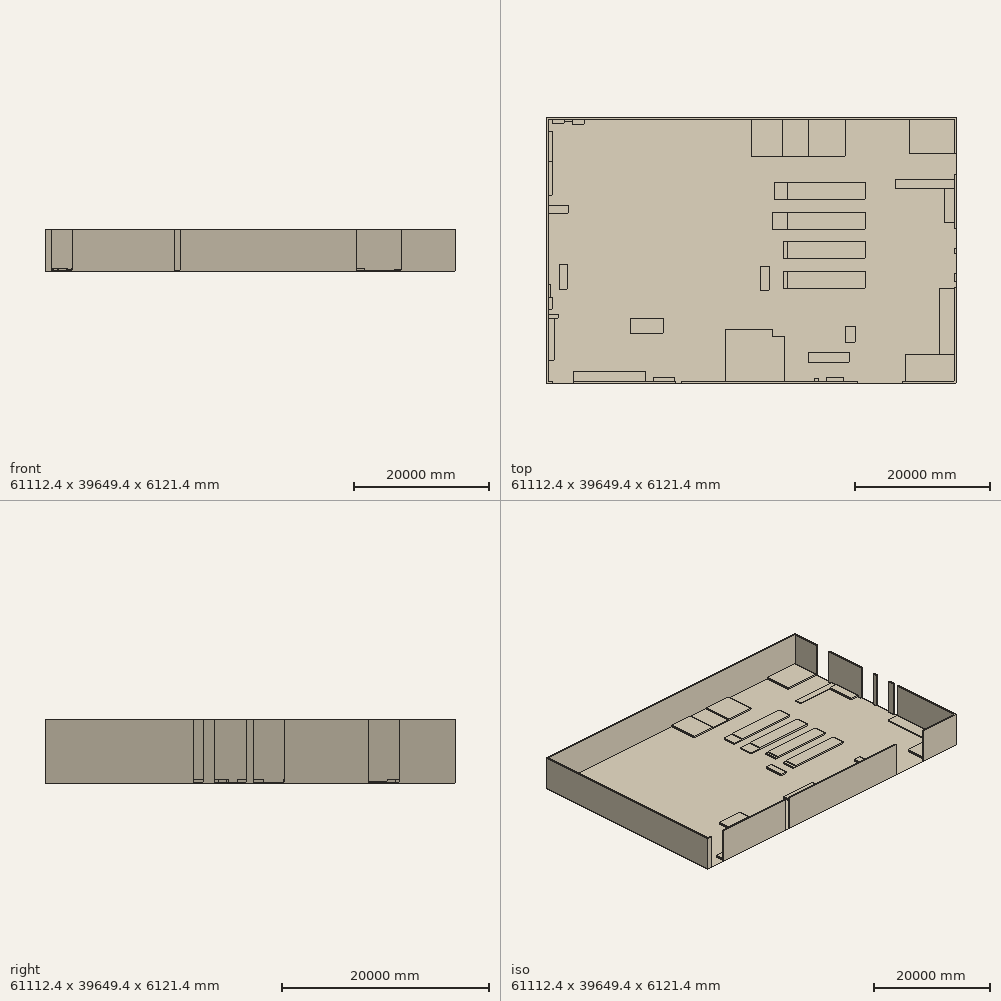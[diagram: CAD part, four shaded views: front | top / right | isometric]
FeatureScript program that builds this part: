
annotation { "Feature Type Name" : "Feature", "Feature Type Description" : "" }
export const myFeature = defineFeature(function(context is Context, id is Id, definition is map)
    precondition{}
    {
        {
            var Q0;
            Q0=qCreatedBy(makeId("Top.planeOp"),FACE);
            var sketch = newSketch(context, id + "F0", { "sketchPlane" : qUnion([Q0])});
            skLineSegment(sketch, "E0.bottom", {"start": v(30556.2, 19824.7) * mm, "end": v(-30556.2, 19824.7) * mm});
            skLineSegment(sketch, "E0.top", {"start": v(30556.2, -19824.7) * mm, "end": v(22479, -19824.7) * mm});
            skLineSegment(sketch, "E0.left", {"start": v(30556.2, 19824.7) * mm, "end": v(30556.2, 14439.9) * mm});
            skLineSegment(sketch, "E0.right", {"start": v(-30556.2, 19824.7) * mm, "end": v(-30556.2, -19824.7) * mm});
            skPoint(sketch, "E0.middle", {"position": v(0, 0) * mm});
            skPoint(sketch, "E1", {"position": v(30556.2, 18148.3) * mm});
            skPoint(sketch, "E2", {"position": v(30556.2, 15100.3) * mm});
            skPoint(sketch, "E3", {"position": v(30556.2, 14439.9) * mm});
            skPoint(sketch, "E4", {"position": v(30556.2, 11391.9) * mm});
            skPoint(sketch, "E5", {"position": v(30556.2, 10731.5) * mm});
            skPoint(sketch, "E6", {"position": v(30556.2, 7683.5) * mm});
            skPoint(sketch, "E7", {"position": v(30556.2, 7023.1) * mm});
            skPoint(sketch, "E8", {"position": v(30556.2, 3975.1) * mm});
            skPoint(sketch, "E9", {"position": v(30556.2, 3314.7) * mm});
            skPoint(sketch, "E10", {"position": v(30556.2, 266.7) * mm});
            skPoint(sketch, "E11", {"position": v(30556.2, -393.7) * mm});
            skPoint(sketch, "E12", {"position": v(30556.2, -3441.7) * mm});
            skPoint(sketch, "E13", {"position": v(30556.2, -4584.7) * mm});
            skPoint(sketch, "E14", {"position": v(30556.2, -5499.1) * mm});
            skPoint(sketch, "E15", {"position": v(-29641.8, -19824.7) * mm});
            skPoint(sketch, "E16", {"position": v(-26593.8, -19824.7) * mm});
            skPoint(sketch, "E17", {"position": v(-11353.8, -19824.7) * mm});
            skPoint(sketch, "E18", {"position": v(-10439.4, -19824.7) * mm});
            skPoint(sketch, "E19", {"position": v(15773.4, -19824.7) * mm});
            skPoint(sketch, "E20", {"position": v(22479, -19824.7) * mm});
            skLineSegment(sketch, "E21.0", {"start": v(30302.2, -19570.7) * mm, "end": v(22479, -19570.7) * mm});
            skLineSegment(sketch, "E21.1", {"start": v(30302.2, 19570.7) * mm, "end": v(30302.2, 14439.9) * mm});
            skLineSegment(sketch, "E21.2", {"start": v(30302.2, 19570.7) * mm, "end": v(-30302.2, 19570.7) * mm});
            skLineSegment(sketch, "E21.3", {"start": v(-30302.2, 19570.7) * mm, "end": v(-30302.2, -19570.7) * mm});
            skLineSegment(sketch, "E22", {"start": v(30556.2, 18148.3) * mm, "end": v(30302.2, 18148.3) * mm});
            skLineSegment(sketch, "E23", {"start": v(30556.2, 15100.3) * mm, "end": v(30302.2, 15100.3) * mm});
            skLineSegment(sketch, "E24", {"start": v(30556.2, 14439.9) * mm, "end": v(30302.2, 14439.9) * mm});
            skLineSegment(sketch, "E25", {"start": v(30556.2, 11391.9) * mm, "end": v(30302.2, 11391.9) * mm});
            skLineSegment(sketch, "E26", {"start": v(30556.2, 10731.5) * mm, "end": v(30302.2, 10731.5) * mm});
            skLineSegment(sketch, "E27", {"start": v(30556.2, 7683.5) * mm, "end": v(30302.2, 7683.5) * mm});
            skLineSegment(sketch, "E28", {"start": v(30556.2, 7023.1) * mm, "end": v(30302.2, 7023.1) * mm});
            skLineSegment(sketch, "E29", {"start": v(30556.2, 3975.1) * mm, "end": v(30302.2, 3975.1) * mm});
            skLineSegment(sketch, "E30", {"start": v(30556.2, 3314.7) * mm, "end": v(30302.2, 3314.7) * mm});
            skLineSegment(sketch, "E31", {"start": v(30556.2, 266.7) * mm, "end": v(30302.2, 266.7) * mm});
            skLineSegment(sketch, "E32", {"start": v(30556.2, -393.7) * mm, "end": v(30302.2, -393.7) * mm});
            skLineSegment(sketch, "E33", {"start": v(30556.2, -3441.7) * mm, "end": v(30302.2, -3441.7) * mm});
            skLineSegment(sketch, "E34", {"start": v(30556.2, -4584.7) * mm, "end": v(30302.2, -4584.7) * mm});
            skLineSegment(sketch, "E35", {"start": v(30556.2, -5499.1) * mm, "end": v(30302.2, -5499.1) * mm});
            skLineSegment(sketch, "E36", {"start": v(22479, -19824.7) * mm, "end": v(22479, -19570.7) * mm});
            skLineSegment(sketch, "E37", {"start": v(15773.4, -19824.7) * mm, "end": v(15773.4, -19570.7) * mm});
            skLineSegment(sketch, "E38", {"start": v(-10439.4, -19824.7) * mm, "end": v(-10439.4, -19570.7) * mm});
            skLineSegment(sketch, "E39", {"start": v(-11353.8, -19824.7) * mm, "end": v(-11353.8, -19570.7) * mm});
            skLineSegment(sketch, "E40", {"start": v(-26593.8, -19824.7) * mm, "end": v(-26593.8, -19570.7) * mm});
            skLineSegment(sketch, "E41", {"start": v(-29641.8, -19824.7) * mm, "end": v(-29641.8, -19570.7) * mm});
            skLineSegment(sketch, "E42.trimOffspring", {"start": v(-29641.8, -19824.7) * mm, "end": v(-30556.2, -19824.7) * mm});
            skLineSegment(sketch, "E43.trimOffspring", {"start": v(-29641.8, -19570.7) * mm, "end": v(-30302.2, -19570.7) * mm});
            skLineSegment(sketch, "E44.trimOffspring", {"start": v(-11353.8, -19824.7) * mm, "end": v(-26593.8, -19824.7) * mm});
            skLineSegment(sketch, "E45.trimOffspring", {"start": v(-11353.8, -19570.7) * mm, "end": v(-26593.8, -19570.7) * mm});
            skLineSegment(sketch, "E46.trimOffspring", {"start": v(15773.4, -19824.7) * mm, "end": v(-10439.4, -19824.7) * mm});
            skLineSegment(sketch, "E47.trimOffspring", {"start": v(15773.4, -19570.7) * mm, "end": v(-10439.4, -19570.7) * mm});
            skLineSegment(sketch, "E48.trimOffspring", {"start": v(30556.2, -5499.1) * mm, "end": v(30556.2, -19824.7) * mm});
            skLineSegment(sketch, "E49.trimOffspring", {"start": v(30302.2, -5499.1) * mm, "end": v(30302.2, -19570.7) * mm});
            skLineSegment(sketch, "E50.trimOffspring", {"start": v(30556.2, -3441.7) * mm, "end": v(30556.2, -4584.7) * mm});
            skLineSegment(sketch, "E51.trimOffspring", {"start": v(30302.2, -3441.7) * mm, "end": v(30302.2, -4584.7) * mm});
            skLineSegment(sketch, "E52.trimOffspring", {"start": v(30556.2, 266.7) * mm, "end": v(30556.2, -393.7) * mm});
            skLineSegment(sketch, "E53.trimOffspring", {"start": v(30302.2, 266.7) * mm, "end": v(30302.2, -393.7) * mm});
            skLineSegment(sketch, "E54.trimOffspring", {"start": v(30556.2, 11391.9) * mm, "end": v(30556.2, 3314.7) * mm});
            skLineSegment(sketch, "E55.trimOffspring", {"start": v(30302.2, 11391.9) * mm, "end": v(30302.2, 3314.7) * mm});
            skSolve(sketch);
        }
        {
            var Q0;
            {var subQ4=sQuery(id+"F0.wireOp",EDGE,"E0.bottom");Q0=makeQuery(id+"F0.imprint","IMPRINT",FACE,{"disambiguationData":[TD([[makeQuery(id+"F0.imprint","IMPRINT",EDGE,{"derivedFrom":subQ4}),1.0]])]});}
            var Q1;
            {var subQ0=sQuery(id+"F0.wireOp",EDGE,"E22");Q1=makeQuery(id+"F0.imprint","IMPRINT",FACE,{"disambiguationData":[TD([[makeQuery(id+"F0.imprint","IMPRINT",EDGE,{"derivedFrom":subQ0}),1.0]])]});}
            var Q2;
            {var subQ2=sQuery(id+"F0.wireOp",EDGE,"E23");Q2=makeQuery(id+"F0.imprint","IMPRINT",FACE,{"disambiguationData":[TD([[makeQuery(id+"F0.imprint","IMPRINT",EDGE,{"derivedFrom":subQ2}),1.0]])]});}
            var Q3;
            {var subQ0=sQuery(id+"F0.wireOp",EDGE,"E25");Q3=makeQuery(id+"F0.imprint","IMPRINT",FACE,{"disambiguationData":[TD([[makeQuery(id+"F0.imprint","IMPRINT",EDGE,{"derivedFrom":subQ0}),1.0]])]});}
            var Q4;
            {var subQ0=sQuery(id+"F0.wireOp",EDGE,"E26");Q4=makeQuery(id+"F0.imprint","IMPRINT",FACE,{"disambiguationData":[TD([[makeQuery(id+"F0.imprint","IMPRINT",EDGE,{"derivedFrom":subQ0}),1.0]])]});}
            var Q5;
            {var subQ0=sQuery(id+"F0.wireOp",EDGE,"E27");Q5=makeQuery(id+"F0.imprint","IMPRINT",FACE,{"disambiguationData":[TD([[makeQuery(id+"F0.imprint","IMPRINT",EDGE,{"derivedFrom":subQ0}),1.0]])]});}
            var Q6;
            {var subQ0=sQuery(id+"F0.wireOp",EDGE,"E28");Q6=makeQuery(id+"F0.imprint","IMPRINT",FACE,{"disambiguationData":[TD([[makeQuery(id+"F0.imprint","IMPRINT",EDGE,{"derivedFrom":subQ0}),1.0]])]});}
            var Q7;
            {var subQ0=sQuery(id+"F0.wireOp",EDGE,"E29");Q7=makeQuery(id+"F0.imprint","IMPRINT",FACE,{"disambiguationData":[TD([[makeQuery(id+"F0.imprint","IMPRINT",EDGE,{"derivedFrom":subQ0}),1.0]])]});}
            var Q8;
            Q8=makeQuery(id+"F0.imprint","IMPRINT",FACE,{"disambiguationData":[TD([[makeQuery(id+"F0.imprint","IMPRINT",EDGE,{"derivedFrom":sQuery(id+"F0.wireOp",EDGE,"E31")}),1.0]])]});
            var Q9;
            Q9=makeQuery(id+"F0.imprint","IMPRINT",FACE,{"disambiguationData":[TD([[makeQuery(id+"F0.imprint","IMPRINT",EDGE,{"derivedFrom":sQuery(id+"F0.wireOp",EDGE,"E33")}),1.0]])]});
            var Q10;
            Q10=makeQuery(id+"F0.imprint","IMPRINT",FACE,{"disambiguationData":[TD([[makeQuery(id+"F0.imprint","IMPRINT",EDGE,{"derivedFrom":sQuery(id+"F0.wireOp",EDGE,"E0.top")}),-1.0]])]});
            var Q11;
            Q11=makeQuery(id+"F0.imprint","IMPRINT",FACE,{"disambiguationData":[TD([[makeQuery(id+"F0.imprint","IMPRINT",EDGE,{"derivedFrom":sQuery(id+"F0.wireOp",EDGE,"E37")}),1.0]])]});
            var Q12;
            Q12=makeQuery(id+"F0.imprint","IMPRINT",FACE,{"disambiguationData":[TD([[makeQuery(id+"F0.imprint","IMPRINT",EDGE,{"derivedFrom":sQuery(id+"F0.wireOp",EDGE,"E39")}),1.0]])]});
            extrude(context, id + "F1", {"entities" : qUnion([Q0, Q1, Q2, Q3, Q4, Q5, Q6, Q7, Q8, Q9, Q10, Q11, Q12]), "depth" : 6096 * mm, "offsetDistance" : 25.4 * mm});
        }
        {
            var Q0;
            Q0=qCreatedBy(makeId("Top.planeOp"),FACE);
            var sketch = newSketch(context, id + "F2", { "sketchPlane" : qUnion([Q0])});
            skLineSegment(sketch, "E56.0.0", {"start": v(30556.2, -5499.1) * mm, "end": v(30302.2, -5499.1) * mm, "construction": true});
            skLineSegment(sketch, "E56.0.1", {"start": v(30302.2, -5499.1) * mm, "end": v(30302.2, -19570.7) * mm, "construction": true});
            skLineSegment(sketch, "E56.0.2", {"start": v(30302.2, -19570.7) * mm, "end": v(22479, -19570.7) * mm, "construction": true});
            skLineSegment(sketch, "E56.0.3", {"start": v(22479, -19570.7) * mm, "end": v(22479, -19824.7) * mm, "construction": true});
            skLineSegment(sketch, "E56.0.4", {"start": v(22479, -19824.7) * mm, "end": v(30556.2, -19824.7) * mm, "construction": true});
            skLineSegment(sketch, "E56.0.5", {"start": v(30556.2, -19824.7) * mm, "end": v(30556.2, -5499.1) * mm, "construction": true});
            skLineSegment(sketch, "E57.0.0", {"start": v(-10439.4, -19570.7) * mm, "end": v(-10439.4, -19824.7) * mm, "construction": true});
            skLineSegment(sketch, "E57.0.1", {"start": v(-10439.4, -19824.7) * mm, "end": v(15773.4, -19824.7) * mm, "construction": true});
            skLineSegment(sketch, "E57.0.2", {"start": v(15773.4, -19824.7) * mm, "end": v(15773.4, -19570.7) * mm, "construction": true});
            skLineSegment(sketch, "E57.0.3", {"start": v(15773.4, -19570.7) * mm, "end": v(-10439.4, -19570.7) * mm, "construction": true});
            skLineSegment(sketch, "E58.0.0", {"start": v(-26593.8, -19570.7) * mm, "end": v(-26593.8, -19824.7) * mm, "construction": true});
            skLineSegment(sketch, "E58.0.1", {"start": v(-26593.8, -19824.7) * mm, "end": v(-11353.8, -19824.7) * mm, "construction": true});
            skLineSegment(sketch, "E58.0.2", {"start": v(-11353.8, -19824.7) * mm, "end": v(-11353.8, -19570.7) * mm, "construction": true});
            skLineSegment(sketch, "E58.0.3", {"start": v(-11353.8, -19570.7) * mm, "end": v(-26593.8, -19570.7) * mm, "construction": true});
            skLineSegment(sketch, "E59.0.0", {"start": v(-30302.2, 19570.7) * mm, "end": v(30302.2, 19570.7) * mm, "construction": true});
            skLineSegment(sketch, "E59.0.1", {"start": v(30302.2, 19570.7) * mm, "end": v(30302.2, 14439.9) * mm, "construction": true});
            skLineSegment(sketch, "E59.0.2", {"start": v(30302.2, 14439.9) * mm, "end": v(30556.2, 14439.9) * mm, "construction": true});
            skLineSegment(sketch, "E59.0.3", {"start": v(30556.2, 14439.9) * mm, "end": v(30556.2, 19824.7) * mm, "construction": true});
            skLineSegment(sketch, "E59.0.4", {"start": v(30556.2, 19824.7) * mm, "end": v(-30556.2, 19824.7) * mm, "construction": true});
            skLineSegment(sketch, "E59.0.5", {"start": v(-30556.2, 19824.7) * mm, "end": v(-30556.2, -19824.7) * mm, "construction": true});
            skLineSegment(sketch, "E59.0.6", {"start": v(-30556.2, -19824.7) * mm, "end": v(-29641.8, -19824.7) * mm, "construction": true});
            skLineSegment(sketch, "E59.0.7", {"start": v(-29641.8, -19824.7) * mm, "end": v(-29641.8, -19570.7) * mm, "construction": true});
            skLineSegment(sketch, "E59.0.8", {"start": v(-29641.8, -19570.7) * mm, "end": v(-30302.2, -19570.7) * mm, "construction": true});
            skLineSegment(sketch, "E59.0.9", {"start": v(-30302.2, -19570.7) * mm, "end": v(-30302.2, 19570.7) * mm, "construction": true});
            skLineSegment(sketch, "E60.0.0", {"start": v(30302.2, 11391.9) * mm, "end": v(30302.2, 3314.7) * mm, "construction": true});
            skLineSegment(sketch, "E60.0.1", {"start": v(30302.2, 3314.7) * mm, "end": v(30556.2, 3314.7) * mm, "construction": true});
            skLineSegment(sketch, "E60.0.2", {"start": v(30556.2, 3314.7) * mm, "end": v(30556.2, 11391.9) * mm, "construction": true});
            skLineSegment(sketch, "E60.0.3", {"start": v(30556.2, 11391.9) * mm, "end": v(30302.2, 11391.9) * mm, "construction": true});
            skLineSegment(sketch, "E61.0.0", {"start": v(30302.2, -393.7) * mm, "end": v(30556.2, -393.7) * mm, "construction": true});
            skLineSegment(sketch, "E61.0.1", {"start": v(30556.2, -393.7) * mm, "end": v(30556.2, 266.7) * mm, "construction": true});
            skLineSegment(sketch, "E61.0.2", {"start": v(30556.2, 266.7) * mm, "end": v(30302.2, 266.7) * mm, "construction": true});
            skLineSegment(sketch, "E61.0.3", {"start": v(30302.2, 266.7) * mm, "end": v(30302.2, -393.7) * mm, "construction": true});
            skLineSegment(sketch, "E62.0.0", {"start": v(30302.2, -4584.7) * mm, "end": v(30556.2, -4584.7) * mm, "construction": true});
            skLineSegment(sketch, "E62.0.1", {"start": v(30556.2, -4584.7) * mm, "end": v(30556.2, -3441.7) * mm, "construction": true});
            skLineSegment(sketch, "E62.0.2", {"start": v(30556.2, -3441.7) * mm, "end": v(30302.2, -3441.7) * mm, "construction": true});
            skLineSegment(sketch, "E62.0.3", {"start": v(30302.2, -3441.7) * mm, "end": v(30302.2, -4584.7) * mm, "construction": true});
            skLineSegment(sketch, "E63.bottom", {"start": v(22987, -19570.7) * mm, "end": v(30302.2, -19570.7) * mm});
            skLineSegment(sketch, "E63.top", {"start": v(22987, -15506.7) * mm, "end": v(28041.6, -15506.7) * mm});
            skLineSegment(sketch, "E63.left", {"start": v(22987, -19570.7) * mm, "end": v(22987, -15506.7) * mm});
            skLineSegment(sketch, "E63.right", {"start": v(30302.2, -19570.7) * mm, "end": v(30302.2, -15506.7) * mm});
            skLineSegment(sketch, "E64.bottom", {"start": v(30302.2, -15506.7) * mm, "end": v(28041.6, -15506.7) * mm});
            skLineSegment(sketch, "E64.top", {"start": v(30302.2, -5600.7) * mm, "end": v(28041.6, -5600.7) * mm});
            skLineSegment(sketch, "E64.left", {"start": v(30302.2, -15506.7) * mm, "end": v(30302.2, -5600.7) * mm});
            skLineSegment(sketch, "E64.right", {"start": v(28041.6, -15506.7) * mm, "end": v(28041.6, -5600.7) * mm});
            skLineSegment(sketch, "E65.bottom", {"start": v(30302.2, 9309.1) * mm, "end": v(21513.8, 9309.1) * mm});
            skLineSegment(sketch, "E65.top", {"start": v(30302.2, 10579.1) * mm, "end": v(21513.8, 10579.1) * mm});
            skLineSegment(sketch, "E65.left", {"start": v(30302.2, 9309.1) * mm, "end": v(30302.2, 10579.1) * mm});
            skLineSegment(sketch, "E65.right", {"start": v(21513.8, 9309.1) * mm, "end": v(21513.8, 10579.1) * mm});
            skLineSegment(sketch, "E66.top", {"start": v(30302.2, 4127.5) * mm, "end": v(28702, 4127.5) * mm});
            skLineSegment(sketch, "E66.left", {"start": v(30302.2, 9309.1) * mm, "end": v(30302.2, 4127.5) * mm});
            skLineSegment(sketch, "E66.right", {"start": v(28702, 9309.1) * mm, "end": v(28702, 4127.5) * mm});
            skLineSegment(sketch, "E67.bottom", {"start": v(30302.2, 14465.3) * mm, "end": v(23520.4, 14465.3) * mm});
            skLineSegment(sketch, "E67.top", {"start": v(30302.2, 19570.7) * mm, "end": v(23520.4, 19570.7) * mm});
            skLineSegment(sketch, "E67.left", {"start": v(30302.2, 14465.3) * mm, "end": v(30302.2, 19570.7) * mm});
            skLineSegment(sketch, "E67.right", {"start": v(23520.4, 14465.3) * mm, "end": v(23520.4, 19570.7) * mm});
            skLineSegment(sketch, "E68.bottom", {"start": v(14541.5, -16675.1) * mm, "end": v(8445.5, -16675.1) * mm});
            skLineSegment(sketch, "E68.top", {"start": v(14541.5, -15252.7) * mm, "end": v(8445.5, -15252.7) * mm});
            skLineSegment(sketch, "E68.left", {"start": v(14541.5, -16675.1) * mm, "end": v(14541.5, -15252.7) * mm});
            skLineSegment(sketch, "E68.right", {"start": v(8445.5, -16675.1) * mm, "end": v(8445.5, -15252.7) * mm});
            skLineSegment(sketch, "E69.bottom", {"start": v(14084.3, -11290.3) * mm, "end": v(15430.5, -11290.3) * mm});
            skLineSegment(sketch, "E69.top", {"start": v(14084.3, -13728.7) * mm, "end": v(15430.5, -13728.7) * mm});
            skLineSegment(sketch, "E69.left", {"start": v(14084.3, -11290.3) * mm, "end": v(14084.3, -13728.7) * mm});
            skLineSegment(sketch, "E69.right", {"start": v(15430.5, -11290.3) * mm, "end": v(15430.5, -13728.7) * mm});
            skLineSegment(sketch, "E70.bottom", {"start": v(17018, -5676.9) * mm, "end": v(5359.4, -5676.9) * mm});
            skLineSegment(sketch, "E70.top", {"start": v(17018, -3136.9) * mm, "end": v(5359.4, -3136.9) * mm});
            skLineSegment(sketch, "E70.left", {"start": v(17018, -5676.9) * mm, "end": v(17018, -3136.9) * mm});
            skLineSegment(sketch, "E70.right", {"start": v(5359.4, -5676.9) * mm, "end": v(5359.4, -3136.9) * mm});
            skLineSegment(sketch, "E71.bottom", {"start": v(17018, -1257.3) * mm, "end": v(5359.4, -1257.3) * mm});
            skLineSegment(sketch, "E71.top", {"start": v(17018, 1282.7) * mm, "end": v(5359.4, 1282.7) * mm});
            skLineSegment(sketch, "E71.left", {"start": v(17018, -1257.3) * mm, "end": v(17018, 1282.7) * mm});
            skLineSegment(sketch, "E71.right", {"start": v(5359.4, -1257.3) * mm, "end": v(5359.4, 1282.7) * mm});
            skLineSegment(sketch, "E72.bottom", {"start": v(17018, 3162.3) * mm, "end": v(5359.4, 3162.3) * mm});
            skLineSegment(sketch, "E72.top", {"start": v(17018, 5702.3) * mm, "end": v(5359.4, 5702.3) * mm});
            skLineSegment(sketch, "E72.left", {"start": v(17018, 3162.3) * mm, "end": v(17018, 5702.3) * mm});
            skLineSegment(sketch, "E72.right", {"start": v(5359.4, 3162.3) * mm, "end": v(5359.4, 5702.3) * mm});
            skLineSegment(sketch, "E73.bottom", {"start": v(17018, 7581.9) * mm, "end": v(5359.4, 7581.9) * mm});
            skLineSegment(sketch, "E73.top", {"start": v(17018, 10121.9) * mm, "end": v(5359.4, 10121.9) * mm});
            skLineSegment(sketch, "E73.left", {"start": v(17018, 7581.9) * mm, "end": v(17018, 10121.9) * mm});
            skLineSegment(sketch, "E73.right", {"start": v(5359.4, 7581.9) * mm, "end": v(5359.4, 10121.9) * mm});
            skLineSegment(sketch, "E74.bottom", {"start": v(-18034, -10198.1) * mm, "end": v(-13055.6, -10198.1) * mm});
            skLineSegment(sketch, "E74.top", {"start": v(-18034, -12331.7) * mm, "end": v(-13055.6, -12331.7) * mm});
            skLineSegment(sketch, "E74.left", {"start": v(-18034, -10198.1) * mm, "end": v(-18034, -12331.7) * mm});
            skLineSegment(sketch, "E74.right", {"start": v(-13055.6, -10198.1) * mm, "end": v(-13055.6, -12331.7) * mm});
            skLineSegment(sketch, "E75.bottom", {"start": v(-26492.2, -19570.7) * mm, "end": v(-15773.4, -19570.7) * mm});
            skLineSegment(sketch, "E75.top", {"start": v(-26492.2, -17970.5) * mm, "end": v(-15773.4, -17970.5) * mm});
            skLineSegment(sketch, "E75.left", {"start": v(-26492.2, -19570.7) * mm, "end": v(-26492.2, -17970.5) * mm});
            skLineSegment(sketch, "E75.right", {"start": v(-15773.4, -19570.7) * mm, "end": v(-15773.4, -17970.5) * mm});
            skLineSegment(sketch, "E76.bottom", {"start": v(-30302.2, -16446.5) * mm, "end": v(-29362.4, -16446.5) * mm});
            skLineSegment(sketch, "E76.top", {"start": v(-30302.2, -10172.7) * mm, "end": v(-29362.4, -10172.7) * mm});
            skLineSegment(sketch, "E76.left", {"start": v(-30302.2, -16446.5) * mm, "end": v(-30302.2, -10172.7) * mm});
            skLineSegment(sketch, "E76.right", {"start": v(-29362.4, -16446.5) * mm, "end": v(-29362.4, -10172.7) * mm});
            skLineSegment(sketch, "E77.bottom", {"start": v(-28676.6, -5803.9) * mm, "end": v(-27432, -5803.9) * mm});
            skLineSegment(sketch, "E77.top", {"start": v(-28676.6, -2146.3) * mm, "end": v(-27432, -2146.3) * mm});
            skLineSegment(sketch, "E77.left", {"start": v(-28676.6, -5803.9) * mm, "end": v(-28676.6, -2146.3) * mm});
            skLineSegment(sketch, "E77.right", {"start": v(-27432, -5803.9) * mm, "end": v(-27432, -2146.3) * mm});
            skLineSegment(sketch, "E78.bottom", {"start": v(-29718, 19570.7) * mm, "end": v(-27889.2, 19570.7) * mm});
            skLineSegment(sketch, "E78.top", {"start": v(-29718, 18986.5) * mm, "end": v(-27889.2, 18986.5) * mm});
            skLineSegment(sketch, "E78.left", {"start": v(-29718, 19570.7) * mm, "end": v(-29718, 18986.5) * mm});
            skLineSegment(sketch, "E78.right", {"start": v(-27889.2, 19570.7) * mm, "end": v(-27889.2, 18986.5) * mm});
            skLineSegment(sketch, "E79.bottom", {"start": v(-30302.2, 17792.7) * mm, "end": v(-29591, 17792.7) * mm});
            skLineSegment(sketch, "E79.top", {"start": v(-30302.2, 8128) * mm, "end": v(-29591, 8128) * mm});
            skLineSegment(sketch, "E79.left", {"start": v(-30302.2, 17792.7) * mm, "end": v(-30302.2, 8128) * mm});
            skLineSegment(sketch, "E79.right", {"start": v(-29591, 17792.7) * mm, "end": v(-29591, 8128) * mm});
            skLineSegment(sketch, "E80.bottom", {"start": v(13970, 19570.7) * mm, "end": v(8458.2, 19570.7) * mm});
            skLineSegment(sketch, "E80.top", {"start": v(13970, 14058.9) * mm, "end": v(8458.2, 14058.9) * mm});
            skLineSegment(sketch, "E80.left", {"start": v(13970, 19570.7) * mm, "end": v(13970, 14058.9) * mm});
            skLineSegment(sketch, "E80.right", {"start": v(8458.2, 19570.7) * mm, "end": v(8458.2, 14058.9) * mm});
            skLineSegment(sketch, "E81.bottom", {"start": v(8458.2, 19570.7) * mm, "end": v(4546.6, 19570.7) * mm});
            skLineSegment(sketch, "E81.top", {"start": v(8458.2, 14058.9) * mm, "end": v(4546.6, 14058.9) * mm});
            skLineSegment(sketch, "E81.right", {"start": v(4546.6, 19570.7) * mm, "end": v(4546.6, 14058.9) * mm});
            skLineSegment(sketch, "E82.bottom", {"start": v(4546.6, 19570.7) * mm, "end": v(-25.4, 19570.7) * mm});
            skLineSegment(sketch, "E82.top", {"start": v(4546.6, 14058.9) * mm, "end": v(-25.4, 14058.9) * mm});
            skLineSegment(sketch, "E82.right", {"start": v(-25.4, 19570.7) * mm, "end": v(-25.4, 14058.9) * mm});
            skLineSegment(sketch, "E83.bottom", {"start": v(-11531.6, -19570.7) * mm, "end": v(-14579.6, -19570.7) * mm});
            skLineSegment(sketch, "E83.top", {"start": v(-11531.6, -18961.1) * mm, "end": v(-14579.6, -18961.1) * mm});
            skLineSegment(sketch, "E83.left", {"start": v(-11531.6, -19570.7) * mm, "end": v(-11531.6, -18961.1) * mm});
            skLineSegment(sketch, "E83.right", {"start": v(-14579.6, -19570.7) * mm, "end": v(-14579.6, -18961.1) * mm});
            skLineSegment(sketch, "E84.bottom", {"start": v(13690.6, -19570.7) * mm, "end": v(11125.2, -19570.7) * mm});
            skLineSegment(sketch, "E84.top", {"start": v(13690.6, -18961.1) * mm, "end": v(11125.2, -18961.1) * mm});
            skLineSegment(sketch, "E84.left", {"start": v(13690.6, -19570.7) * mm, "end": v(13690.6, -18961.1) * mm});
            skLineSegment(sketch, "E84.right", {"start": v(11125.2, -19570.7) * mm, "end": v(11125.2, -18961.1) * mm});
            skLineSegment(sketch, "E85.bottom", {"start": v(5359.4, 3162.3) * mm, "end": v(3073.4, 3162.3) * mm});
            skLineSegment(sketch, "E85.top", {"start": v(5359.4, 5702.3) * mm, "end": v(3073.4, 5702.3) * mm});
            skLineSegment(sketch, "E85.right", {"start": v(3073.4, 3162.3) * mm, "end": v(3073.4, 5702.3) * mm});
            skLineSegment(sketch, "E86.bottom", {"start": v(5359.4, 1282.7) * mm, "end": v(4826, 1282.7) * mm});
            skLineSegment(sketch, "E86.top", {"start": v(5359.4, -1257.3) * mm, "end": v(4826, -1257.3) * mm});
            skLineSegment(sketch, "E86.left", {"start": v(5359.4, 1282.7) * mm, "end": v(5359.4, -1257.3) * mm});
            skLineSegment(sketch, "E86.right", {"start": v(4826, 1282.7) * mm, "end": v(4826, -1257.3) * mm});
            skLineSegment(sketch, "E87.bottom", {"start": v(5359.4, -5676.9) * mm, "end": v(4749.8, -5676.9) * mm});
            skLineSegment(sketch, "E87.top", {"start": v(5359.4, -3136.9) * mm, "end": v(4749.8, -3136.9) * mm});
            skLineSegment(sketch, "E87.right", {"start": v(4749.8, -5676.9) * mm, "end": v(4749.8, -3136.9) * mm});
            skLineSegment(sketch, "E88.bottom", {"start": v(-30302.2, -6997.7) * mm, "end": v(-29895.8, -6997.7) * mm});
            skLineSegment(sketch, "E88.top", {"start": v(-30302.2, -5067.3) * mm, "end": v(-29895.8, -5067.3) * mm});
            skLineSegment(sketch, "E88.left", {"start": v(-30302.2, -6997.7) * mm, "end": v(-30302.2, -5067.3) * mm});
            skLineSegment(sketch, "E88.right", {"start": v(-29895.8, -6997.7) * mm, "end": v(-29895.8, -5067.3) * mm});
            skLineSegment(sketch, "E89.bottom", {"start": v(2616.2, -5981.7) * mm, "end": v(1397, -5981.7) * mm});
            skLineSegment(sketch, "E89.top", {"start": v(2616.2, -2324.1) * mm, "end": v(1397, -2324.1) * mm});
            skLineSegment(sketch, "E89.left", {"start": v(2616.2, -5981.7) * mm, "end": v(2616.2, -2324.1) * mm});
            skLineSegment(sketch, "E89.right", {"start": v(1397, -5981.7) * mm, "end": v(1397, -2324.1) * mm});
            skLineSegment(sketch, "E90.bottom", {"start": v(5359.4, 10121.9) * mm, "end": v(3378.2, 10121.9) * mm});
            skLineSegment(sketch, "E90.top", {"start": v(5359.4, 7581.9) * mm, "end": v(3378.2, 7581.9) * mm});
            skLineSegment(sketch, "E90.left", {"start": v(5359.4, 10121.9) * mm, "end": v(5359.4, 7581.9) * mm});
            skLineSegment(sketch, "E90.right", {"start": v(3378.2, 10121.9) * mm, "end": v(3378.2, 7581.9) * mm});
            skLineSegment(sketch, "E91.bottom", {"start": v(17018, 10121.9) * mm, "end": v(15798.8, 10121.9) * mm});
            skLineSegment(sketch, "E91.top", {"start": v(17018, 10934.7) * mm, "end": v(15798.8, 10934.7) * mm});
            skLineSegment(sketch, "E91.left", {"start": v(17018, 10121.9) * mm, "end": v(17018, 10934.7) * mm});
            skLineSegment(sketch, "E91.right", {"start": v(15798.8, 10121.9) * mm, "end": v(15798.8, 10934.7) * mm});
            skLineSegment(sketch, "E92.bottom", {"start": v(-30302.2, -10172.7) * mm, "end": v(-28778.2, -10172.7) * mm});
            skLineSegment(sketch, "E92.top", {"start": v(-30302.2, -9486.9) * mm, "end": v(-28778.2, -9486.9) * mm});
            skLineSegment(sketch, "E92.left", {"start": v(-30302.2, -10172.7) * mm, "end": v(-30302.2, -9486.9) * mm});
            skLineSegment(sketch, "E92.right", {"start": v(-28778.2, -10172.7) * mm, "end": v(-28778.2, -9486.9) * mm});
            skLineSegment(sketch, "E93", {"start": v(-29591, 13220.7) * mm, "end": v(-30302.2, 13220.7) * mm});
            skLineSegment(sketch, "E94.bottom", {"start": v(-26670, 19570.7) * mm, "end": v(-24841.2, 19570.7) * mm});
            skLineSegment(sketch, "E94.top", {"start": v(-26670, 18808.7) * mm, "end": v(-24841.2, 18808.7) * mm});
            skLineSegment(sketch, "E94.left", {"start": v(-26670, 19570.7) * mm, "end": v(-26670, 18808.7) * mm});
            skLineSegment(sketch, "E94.right", {"start": v(-24841.2, 19570.7) * mm, "end": v(-24841.2, 18808.7) * mm});
            skLineSegment(sketch, "E95.bottom", {"start": v(-30302.2, -6997.7) * mm, "end": v(-29641.8, -6997.7) * mm});
            skLineSegment(sketch, "E95.top", {"start": v(-30302.2, -8826.5) * mm, "end": v(-29641.8, -8826.5) * mm});
            skLineSegment(sketch, "E95.left", {"start": v(-30302.2, -6997.7) * mm, "end": v(-30302.2, -8826.5) * mm});
            skLineSegment(sketch, "E95.right", {"start": v(-29641.8, -6997.7) * mm, "end": v(-29641.8, -8826.5) * mm});
            skLineSegment(sketch, "E96.bottom", {"start": v(-30302.2, 6705.6) * mm, "end": v(-27254.2, 6705.6) * mm});
            skLineSegment(sketch, "E96.top", {"start": v(-30302.2, 5562.6) * mm, "end": v(-27254.2, 5562.6) * mm});
            skLineSegment(sketch, "E96.left", {"start": v(-30302.2, 6705.6) * mm, "end": v(-30302.2, 5562.6) * mm});
            skLineSegment(sketch, "E96.right", {"start": v(-27254.2, 6705.6) * mm, "end": v(-27254.2, 5562.6) * mm});
            skLineSegment(sketch, "E97.bottom", {"start": v(-29514.8, 5562.6) * mm, "end": v(-27990.8, 5562.6) * mm});
            skLineSegment(sketch, "E97.top", {"start": v(-29514.8, 5257.8) * mm, "end": v(-27990.8, 5257.8) * mm});
            skLineSegment(sketch, "E97.left", {"start": v(-29514.8, 5562.6) * mm, "end": v(-29514.8, 5257.8) * mm});
            skLineSegment(sketch, "E97.right", {"start": v(-27990.8, 5562.6) * mm, "end": v(-27990.8, 5257.8) * mm});
            skLineSegment(sketch, "E98.bottom", {"start": v(-27889.2, 19265.9) * mm, "end": v(-26670, 19265.9) * mm});
            skLineSegment(sketch, "E98.top", {"start": v(-27889.2, 19570.7) * mm, "end": v(-26670, 19570.7) * mm});
            skLineSegment(sketch, "E98.left", {"start": v(-27889.2, 19265.9) * mm, "end": v(-27889.2, 19570.7) * mm});
            skLineSegment(sketch, "E98.right", {"start": v(-26670, 19265.9) * mm, "end": v(-26670, 19570.7) * mm});
            skLineSegment(sketch, "E99.bottom", {"start": v(9982.2, -19570.7) * mm, "end": v(9321.8, -19570.7) * mm});
            skLineSegment(sketch, "E99.top", {"start": v(9982.2, -19151.6) * mm, "end": v(9321.8, -19151.6) * mm});
            skLineSegment(sketch, "E99.left", {"start": v(9982.2, -19570.7) * mm, "end": v(9982.2, -19151.6) * mm});
            skLineSegment(sketch, "E99.right", {"start": v(9321.8, -19570.7) * mm, "end": v(9321.8, -19151.6) * mm});
            skLineSegment(sketch, "E100.bottom", {"start": v(4940.3, -19570.7) * mm, "end": v(-3816.35, -19570.7) * mm});
            skLineSegment(sketch, "E100.top", {"start": v(3200.4, -11760.2) * mm, "end": v(-3816.35, -11760.2) * mm});
            skLineSegment(sketch, "E100.left", {"start": v(4940.3, -19570.7) * mm, "end": v(4940.3, -12776.2) * mm});
            skLineSegment(sketch, "E100.right", {"start": v(-3816.35, -19570.7) * mm, "end": v(-3816.35, -11760.2) * mm});
            skLineSegment(sketch, "E101.top", {"start": v(4940.3, -12776.2) * mm, "end": v(3200.4, -12776.2) * mm});
            skLineSegment(sketch, "E101.right", {"start": v(3200.4, -11760.2) * mm, "end": v(3200.4, -12776.2) * mm});
            skSolve(sketch);
        }
        {
            var Q0;
            Q0=makeQuery(id+"F2.imprint","IMPRINT",FACE,{"disambiguationData":[TD([[makeQuery(id+"F2.imprint","IMPRINT",EDGE,{"derivedFrom":sQuery(id+"F2.wireOp",EDGE,"E78.bottom")}),-1.0]])]});
            var Q1;
            Q1=makeQuery(id+"F2.imprint","IMPRINT",FACE,{"disambiguationData":[TD([[makeQuery(id+"F2.imprint","IMPRINT",EDGE,{"derivedFrom":sQuery(id+"F2.wireOp",EDGE,"E94.bottom")}),-1.0]])]});
            var Q2;
            {var subQ0=sQuery(id+"F2.wireOp",EDGE,"E79.bottom");Q2=makeQuery(id+"F2.imprint","IMPRINT",FACE,{"disambiguationData":[TD([[makeQuery(id+"F2.imprint","IMPRINT",EDGE,{"derivedFrom":subQ0}),-1.0]])]});}
            var Q3;
            Q3=makeQuery(id+"F2.imprint","IMPRINT",FACE,{"disambiguationData":[TD([[makeQuery(id+"F2.imprint","IMPRINT",EDGE,{"derivedFrom":sQuery(id+"F2.wireOp",EDGE,"E96.bottom")}),-1.0]])]});
            var Q4;
            Q4=makeQuery(id+"F2.imprint","IMPRINT",FACE,{"disambiguationData":[TD([[makeQuery(id+"F2.imprint","IMPRINT",EDGE,{"derivedFrom":sQuery(id+"F2.wireOp",EDGE,"E77.bottom")}),1.0]])]});
            var Q5;
            Q5=makeQuery(id+"F2.imprint","IMPRINT",FACE,{"disambiguationData":[TD([[makeQuery(id+"F2.imprint","IMPRINT",EDGE,{"derivedFrom":sQuery(id+"F2.wireOp",EDGE,"E88.top")}),-1.0]])]});
            var Q6;
            Q6=makeQuery(id+"F2.imprint","IMPRINT",FACE,{"disambiguationData":[TD([[makeQuery(id+"F2.imprint","IMPRINT",EDGE,{"derivedFrom":sQuery(id+"F2.wireOp",EDGE,"E92.top")}),-1.0]])]});
            var Q7;
            Q7=makeQuery(id+"F2.imprint","IMPRINT",FACE,{"disambiguationData":[TD([[makeQuery(id+"F2.imprint","IMPRINT",EDGE,{"derivedFrom":sQuery(id+"F2.wireOp",EDGE,"E75.bottom")}),1.0]])]});
            var Q8;
            Q8=makeQuery(id+"F2.imprint","IMPRINT",FACE,{"disambiguationData":[TD([[makeQuery(id+"F2.imprint","IMPRINT",EDGE,{"derivedFrom":sQuery(id+"F2.wireOp",EDGE,"E83.bottom")}),-1.0]])]});
            var Q9;
            Q9=makeQuery(id+"F2.imprint","IMPRINT",FACE,{"disambiguationData":[TD([[makeQuery(id+"F2.imprint","IMPRINT",EDGE,{"derivedFrom":sQuery(id+"F2.wireOp",EDGE,"E74.bottom")}),-1.0]])]});
            var Q10;
            Q10=makeQuery(id+"F2.imprint","IMPRINT",FACE,{"disambiguationData":[TD([[makeQuery(id+"F2.imprint","IMPRINT",EDGE,{"derivedFrom":sQuery(id+"F2.wireOp",EDGE,"E84.bottom")}),-1.0]])]});
            var Q11;
            Q11=makeQuery(id+"F2.imprint","IMPRINT",FACE,{"disambiguationData":[TD([[makeQuery(id+"F2.imprint","IMPRINT",EDGE,{"derivedFrom":sQuery(id+"F2.wireOp",EDGE,"E68.bottom")}),-1.0]])]});
            var Q12;
            Q12=makeQuery(id+"F2.imprint","IMPRINT",FACE,{"disambiguationData":[TD([[makeQuery(id+"F2.imprint","IMPRINT",EDGE,{"derivedFrom":sQuery(id+"F2.wireOp",EDGE,"E69.bottom")}),-1.0]])]});
            var Q13;
            Q13=makeQuery(id+"F2.imprint","IMPRINT",FACE,{"disambiguationData":[TD([[makeQuery(id+"F2.imprint","IMPRINT",EDGE,{"derivedFrom":sQuery(id+"F2.wireOp",EDGE,"E63.bottom")}),1.0]])]});
            var Q14;
            Q14=makeQuery(id+"F2.imprint","IMPRINT",FACE,{"disambiguationData":[TD([[makeQuery(id+"F2.imprint","IMPRINT",EDGE,{"derivedFrom":sQuery(id+"F2.wireOp",EDGE,"E70.bottom")}),-1.0]])]});
            var Q15;
            Q15=makeQuery(id+"F2.imprint","IMPRINT",FACE,{"disambiguationData":[TD([[makeQuery(id+"F2.imprint","IMPRINT",EDGE,{"derivedFrom":sQuery(id+"F2.wireOp",EDGE,"E71.bottom")}),-1.0]])]});
            var Q16;
            Q16=makeQuery(id+"F2.imprint","IMPRINT",FACE,{"disambiguationData":[TD([[makeQuery(id+"F2.imprint","IMPRINT",EDGE,{"derivedFrom":sQuery(id+"F2.wireOp",EDGE,"E89.bottom")}),-1.0]])]});
            var Q17;
            Q17=makeQuery(id+"F2.imprint","IMPRINT",FACE,{"disambiguationData":[TD([[makeQuery(id+"F2.imprint","IMPRINT",EDGE,{"derivedFrom":sQuery(id+"F2.wireOp",EDGE,"E72.bottom")}),-1.0]])]});
            var Q18;
            Q18=makeQuery(id+"F2.imprint","IMPRINT",FACE,{"disambiguationData":[TD([[makeQuery(id+"F2.imprint","IMPRINT",EDGE,{"derivedFrom":sQuery(id+"F2.wireOp",EDGE,"E73.bottom")}),-1.0]])]});
            var Q19;
            Q19=makeQuery(id+"F2.imprint","IMPRINT",FACE,{"disambiguationData":[TD([[makeQuery(id+"F2.imprint","IMPRINT",EDGE,{"derivedFrom":sQuery(id+"F2.wireOp",EDGE,"E66.top")}),-1.0]])]});
            var Q20;
            Q20=makeQuery(id+"F2.imprint","IMPRINT",FACE,{"disambiguationData":[TD([[makeQuery(id+"F2.imprint","IMPRINT",EDGE,{"derivedFrom":sQuery(id+"F2.wireOp",EDGE,"E67.bottom")}),-1.0]])]});
            var Q21;
            Q21=makeQuery(id+"F2.imprint","IMPRINT",FACE,{"disambiguationData":[TD([[makeQuery(id+"F2.imprint","IMPRINT",EDGE,{"derivedFrom":sQuery(id+"F2.wireOp",EDGE,"E80.bottom")}),1.0]])]});
            var Q22;
            Q22=makeQuery(id+"F2.imprint","IMPRINT",FACE,{"disambiguationData":[TD([[makeQuery(id+"F2.imprint","IMPRINT",EDGE,{"derivedFrom":sQuery(id+"F2.wireOp",EDGE,"E82.bottom")}),1.0]])]});
            var Q23;
            Q23=makeQuery(id+"F2.imprint","IMPRINT",FACE,{"disambiguationData":[TD([[makeQuery(id+"F2.imprint","IMPRINT",EDGE,{"derivedFrom":sQuery(id+"F2.wireOp",EDGE,"E99.bottom")}),-1.0]])]});
            var Q24;
            Q24=makeQuery(id+"F2.imprint","IMPRINT",FACE,{"disambiguationData":[TD([[makeQuery(id+"F2.imprint","IMPRINT",EDGE,{"derivedFrom":sQuery(id+"F2.wireOp",EDGE,"E100.bottom")}),-1.0]])]});
            extrude(context, id + "F3", {"entities" : qUnion([Q0, Q1, Q2, Q3, Q4, Q5, Q6, Q7, Q8, Q9, Q10, Q11, Q12, Q13, Q14, Q15, Q16, Q17, Q18, Q19, Q20, Q21, Q22, Q23, Q24]), "depth" : 304.8 * mm, "offsetDistance" : 25.4 * mm});
        }
        {
            var Q0;
            Q0=makeQuery(id+"F2.imprint","IMPRINT",FACE,{"disambiguationData":[TD([[makeQuery(id+"F2.imprint","IMPRINT",EDGE,{"derivedFrom":sQuery(id+"F2.wireOp",EDGE,"E76.bottom")}),1.0]])]});
            var Q1;
            Q1=makeQuery(id+"F2.imprint","IMPRINT",FACE,{"disambiguationData":[TD([[makeQuery(id+"F2.imprint","IMPRINT",EDGE,{"derivedFrom":sQuery(id+"F2.wireOp",EDGE,"E95.top")}),1.0]])]});
            var Q2;
            Q2=makeQuery(id+"F2.imprint","IMPRINT",FACE,{"disambiguationData":[TD([[makeQuery(id+"F2.imprint","IMPRINT",EDGE,{"derivedFrom":sQuery(id+"F2.wireOp",EDGE,"E97.bottom")}),-1.0]])]});
            var Q3;
            {var subQ0=sQuery(id+"F2.wireOp",EDGE,"E79.top");Q3=makeQuery(id+"F2.imprint","IMPRINT",FACE,{"disambiguationData":[TD([[makeQuery(id+"F2.imprint","IMPRINT",EDGE,{"derivedFrom":subQ0}),1.0]])]});}
            var Q4;
            Q4=makeQuery(id+"F2.imprint","IMPRINT",FACE,{"disambiguationData":[TD([[makeQuery(id+"F2.imprint","IMPRINT",EDGE,{"derivedFrom":sQuery(id+"F2.wireOp",EDGE,"E98.bottom")}),1.0]])]});
            var Q5;
            Q5=makeQuery(id+"F2.imprint","IMPRINT",FACE,{"disambiguationData":[TD([[makeQuery(id+"F2.imprint","IMPRINT",EDGE,{"derivedFrom":sQuery(id+"F2.wireOp",EDGE,"E81.bottom")}),1.0]])]});
            var Q6;
            Q6=makeQuery(id+"F2.imprint","IMPRINT",FACE,{"disambiguationData":[TD([[makeQuery(id+"F2.imprint","IMPRINT",EDGE,{"derivedFrom":sQuery(id+"F2.wireOp",EDGE,"E91.bottom")}),-1.0]])]});
            var Q7;
            Q7=makeQuery(id+"F2.imprint","IMPRINT",FACE,{"disambiguationData":[TD([[makeQuery(id+"F2.imprint","IMPRINT",EDGE,{"derivedFrom":sQuery(id+"F2.wireOp",EDGE,"E90.bottom")}),1.0]])]});
            var Q8;
            Q8=makeQuery(id+"F2.imprint","IMPRINT",FACE,{"disambiguationData":[TD([[makeQuery(id+"F2.imprint","IMPRINT",EDGE,{"derivedFrom":sQuery(id+"F2.wireOp",EDGE,"E65.top")}),1.0]])]});
            var Q9;
            Q9=makeQuery(id+"F2.imprint","IMPRINT",FACE,{"disambiguationData":[TD([[makeQuery(id+"F2.imprint","IMPRINT",EDGE,{"derivedFrom":sQuery(id+"F2.wireOp",EDGE,"E85.bottom")}),-1.0]])]});
            var Q10;
            Q10=makeQuery(id+"F2.imprint","IMPRINT",FACE,{"disambiguationData":[TD([[makeQuery(id+"F2.imprint","IMPRINT",EDGE,{"derivedFrom":sQuery(id+"F2.wireOp",EDGE,"E86.bottom")}),1.0]])]});
            var Q11;
            Q11=makeQuery(id+"F2.imprint","IMPRINT",FACE,{"disambiguationData":[TD([[makeQuery(id+"F2.imprint","IMPRINT",EDGE,{"derivedFrom":sQuery(id+"F2.wireOp",EDGE,"E87.bottom")}),-1.0]])]});
            var Q12;
            Q12=makeQuery(id+"F2.imprint","IMPRINT",FACE,{"disambiguationData":[TD([[makeQuery(id+"F2.imprint","IMPRINT",EDGE,{"derivedFrom":sQuery(id+"F2.wireOp",EDGE,"E64.bottom")}),-1.0]])]});
            extrude(context, id + "F4", {"entities" : qUnion([Q0, Q1, Q2, Q3, Q4, Q5, Q6, Q7, Q8, Q9, Q10, Q11, Q12]), "depth" : 152.4 * mm, "offsetDistance" : 25.4 * mm});
        }
        {
            var Q0;
            Q0=qCreatedBy(makeId("Top.planeOp"),FACE);
            var sketch = newSketch(context, id + "F5", { "sketchPlane" : qUnion([Q0])});
            skPoint(sketch, "E102.0", {"position": v(-30556.2, 19824.7) * mm});
            skPoint(sketch, "E103.0", {"position": v(30556.2, 19824.7) * mm});
            skPoint(sketch, "E104.0", {"position": v(30556.2, -19824.7) * mm});
            skPoint(sketch, "E105.0", {"position": v(-30556.2, -19824.7) * mm});
            skLineSegment(sketch, "E106.bottom", {"start": v(-30556.2, -19824.7) * mm, "end": v(30556.2, -19824.7) * mm});
            skLineSegment(sketch, "E106.top", {"start": v(-30556.2, 19824.7) * mm, "end": v(30556.2, 19824.7) * mm});
            skLineSegment(sketch, "E106.left", {"start": v(-30556.2, -19824.7) * mm, "end": v(-30556.2, 19824.7) * mm});
            skLineSegment(sketch, "E106.right", {"start": v(30556.2, -19824.7) * mm, "end": v(30556.2, 19824.7) * mm});
            skSolve(sketch);
        }
        {
            var Q0;
            Q0 = qSketchRegion(id + "F5", true);
            extrude(context, id + "F6", {"entities" : qUnion([Q0]), "operationType" : NewBodyOperationType.ADD, "oppositeDirection" : true, "depth" : 25.4 * mm, "offsetDistance" : 25.4 * mm});
        }
    });
